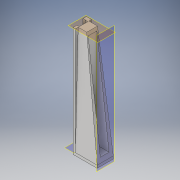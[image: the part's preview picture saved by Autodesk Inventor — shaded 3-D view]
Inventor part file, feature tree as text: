
AUTODESK INVENTOR PART (.ipt)
format: ipt  version: 2019 (Build 230136000, 136)  size: 161,792 bytes
history: native  units: in
note: dims shown in document units (in); Inventor stores cm internally (conversion verified against a paired STEP export)
features: sketch x5, plane x3, extrude x3, loft x1, projected_geometry x1
ambient origin geometry x8: Origin, YZ Plane, XZ Plane, XY Plane, X Axis, Y Axis, Z Axis, Center Point
bodies: Body1 (feature_tree)
feature tree (13):
  sketch  "Sketch5"  dims[d42=1.5in d48=10.0in]
  plane  "Work Plane1"
  loft  "Loft2"
  sketch  "Sketch7"  dims[d58=2.025in d59=0.0in d60=90.0deg]
  plane  "Work Plane2"
  plane  "Work Plane3"
  extrude  "Extrusion10"  Depth=0.25in
  extrude  "Extrusion12"  TaperAngle=0.0deg  [1 undecoded]
  extrude  "Extrusion13"  Depth=0.187in
  sketch  "Sketch6"  dims[d51=1.0in d52=0.8in d53=0.25in]
  sketch  "Sketch10"  dims[d61=0.0in d62=90.0deg d74=0.187in]
  projected_geometry  "Projected Loop3"
  sketch  "Sketch11"  dims[d81=0.252in d82=0.0in d86=0.815in d87=0.3425in d88=1.5in d89=0.7in d90=1.25in d91=0.0in d92=0.475in d93=0.324in d94=0.225in d95=0.355in d96=0.79in d97=0.238in d98=1.0in d99=0.0in]
note: 1 required parameter value undecoded (feature->parameter linkage not recoverable at this tier; creation-order binding heuristic only, values carry confidence <= 0.55)
